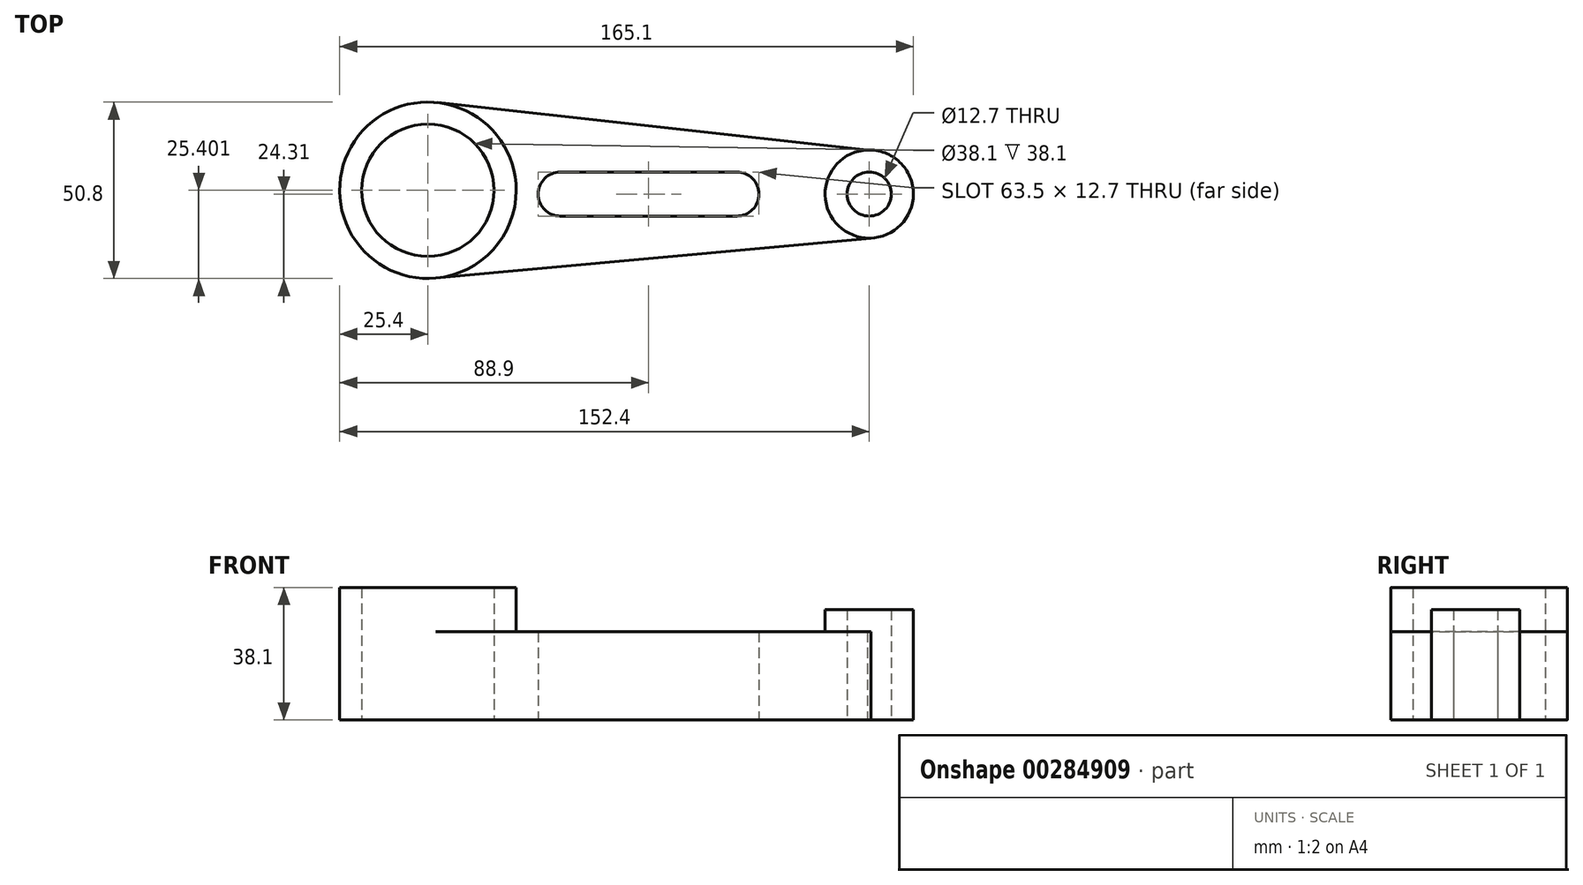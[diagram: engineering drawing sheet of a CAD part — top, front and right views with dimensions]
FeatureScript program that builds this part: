
annotation { "Feature Type Name" : "Feature", "Feature Type Description" : "" }
export const myFeature = defineFeature(function(context is Context, id is Id, definition is map)
    precondition{}
    {
        {
            var Q0;
            Q0=qCreatedBy(makeId("Top.planeOp"),FACE);
            var sketch = newSketch(context, id + "F0", { "sketchPlane" : qUnion([Q0])});
            skCircle(sketch, "E0", {"center": v(-73.86, 1.1) * mm, "radius": 25.4 * mm});
            skCircle(sketch, "E1", {"center": v(53.14, 0) * mm, "radius": 12.7 * mm});
            skLineSegment(sketch, "E2", {"start": v(-71.08, 26.34) * mm, "end": v(52.65, 12.7) * mm});
            skLineSegment(sketch, "E3", {"start": v(53.66, -12.69) * mm, "end": v(-71.53, -24.2) * mm});
            skCircle(sketch, "E4", {"center": v(-73.86, 1.1) * mm, "radius": 19.05 * mm});
            skCircle(sketch, "E5", {"center": v(53.14, 0) * mm, "radius": 6.35 * mm});
            skArc(sketch, "E6", {"start": v(15.04, -6.35) * mm, "mid": v(21.4, 0) * mm, "end": v(15.04, 6.35) * mm});
            skArc(sketch, "E7", {"start": v(-35.76, 6.35) * mm, "mid": v(-42.1, 0) * mm, "end": v(-35.76, -6.35) * mm});
            skLineSegment(sketch, "E8", {"start": v(15.04, 6.35) * mm, "end": v(-35.76, 6.35) * mm});
            skLineSegment(sketch, "E9", {"start": v(-35.76, -6.35) * mm, "end": v(15.04, -6.35) * mm});
            skSolve(sketch);
        }
        {
            var Q0;
            Q0=makeQuery(id+"F0.imprint","IMPRINT",FACE,{"disambiguationData":[TD([[makeQuery(id+"F0.imprint","IMPRINT",EDGE,{"derivedFrom":sQuery(id+"F0.wireOp",EDGE,"E4")}),-1.0]])]});
            var Q1;
            Q1=makeQuery(id+"F0.imprint","IMPRINT",FACE,{"disambiguationData":[TD([[makeQuery(id+"F0.imprint","IMPRINT",EDGE,{"derivedFrom":sQuery(id+"F0.wireOp",EDGE,"E5")}),-1.0]])]});
            var Q2;
            {var subQ1=sQuery(id+"F0.wireOp",EDGE,"E2");Q2=makeQuery(id+"F0.imprint","IMPRINT",FACE,{"disambiguationData":[TD([[makeQuery(id+"F0.imprint","IMPRINT",EDGE,{"derivedFrom":subQ1}),-1.0]])]});}
            extrude(context, id + "F1", {"entities" : qUnion([Q0, Q1, Q2]), "depth" : 25.4 * mm});
        }
        {
            var Q0;
            Q0=makeQuery(id+"F0.imprint","IMPRINT",FACE,{"disambiguationData":[TD([[makeQuery(id+"F0.imprint","IMPRINT",EDGE,{"derivedFrom":sQuery(id+"F0.wireOp",EDGE,"E4")}),-1.0]])]});
            extrude(context, id + "F2", {"entities" : qUnion([Q0]), "operationType" : NewBodyOperationType.ADD, "depth" : 38.1 * mm});
        }
        {
            var Q0;
            Q0=makeQuery(id+"F0.imprint","IMPRINT",FACE,{"disambiguationData":[TD([[makeQuery(id+"F0.imprint","IMPRINT",EDGE,{"derivedFrom":sQuery(id+"F0.wireOp",EDGE,"E5")}),-1.0]])]});
            extrude(context, id + "F3", {"entities" : qUnion([Q0]), "operationType" : NewBodyOperationType.ADD, "depth" : 31.75 * mm});
        }
    });
